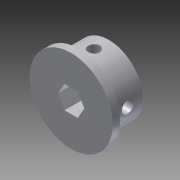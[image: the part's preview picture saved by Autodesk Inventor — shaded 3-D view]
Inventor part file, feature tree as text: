
AUTODESK INVENTOR PART (.ipt)
format: ipt  version: 2014 (Build 180170000, 170)  size: 161,792 bytes
history: native  units: in
note: dims shown in document units (in); Inventor stores cm internally (conversion verified against a paired STEP export)
features: extrude x6, sketch x6, plane x5, fillet x1, projected_geometry x1
ambient origin geometry x8: Origin, YZ Plane, XZ Plane, XY Plane, X Axis, Y Axis, Z Axis, Center Point
bodies: Solid1 (feature_tree)
feature tree (19):
  extrude  "Extrusion1"  Depth=0.379in
  plane  "Work Plane1"
  extrude  "Extrusion2"  Depth=0.5in
  plane  "Work Plane2"
  extrude  "Extrusion3"  Depth=0.25in TaperAngle=0.0deg
  plane  "Work Plane4"
  extrude  "Extrusion4"  Depth=0.25in
  plane  "Work Plane5"
  extrude  "Extrusion5"  TaperAngle=150.0deg  [1 undecoded]
  extrude  "Extrusion6"  Depth=0.0312in
  fillet  "Fillet1"  Radius=0.25in
  sketch  "Sketch1"  dims[d0=1.123in d2=0.379in]
  sketch  "Sketch2"  dims[d3=0.5in d4=0.0in d5=0.19in]
  projected_geometry  "Projected Loop1"
  sketch  "Sketch3"  dims[d6=0.25in d7=0.25in d8=0.0in]
  plane  "Work Plane3"
  sketch  "Sketch4"  dims[d9=0.19in d10=0.25in]
  sketch  "Sketch5"  dims[d11=0.25in d12=0.0in d13=150.0deg]
  sketch  "Sketch6"  dims[d14=0.19in d15=0.25in d16=0.25in d17=0.0in d18=0.19in d19=0.25in d20=0.25in d21=0.0in d22=1.375in d23=0.125in d24=0.0in d25=0.0312in]
note: 1 required parameter value undecoded (feature->parameter linkage not recoverable at this tier; creation-order binding heuristic only, values carry confidence <= 0.55)
